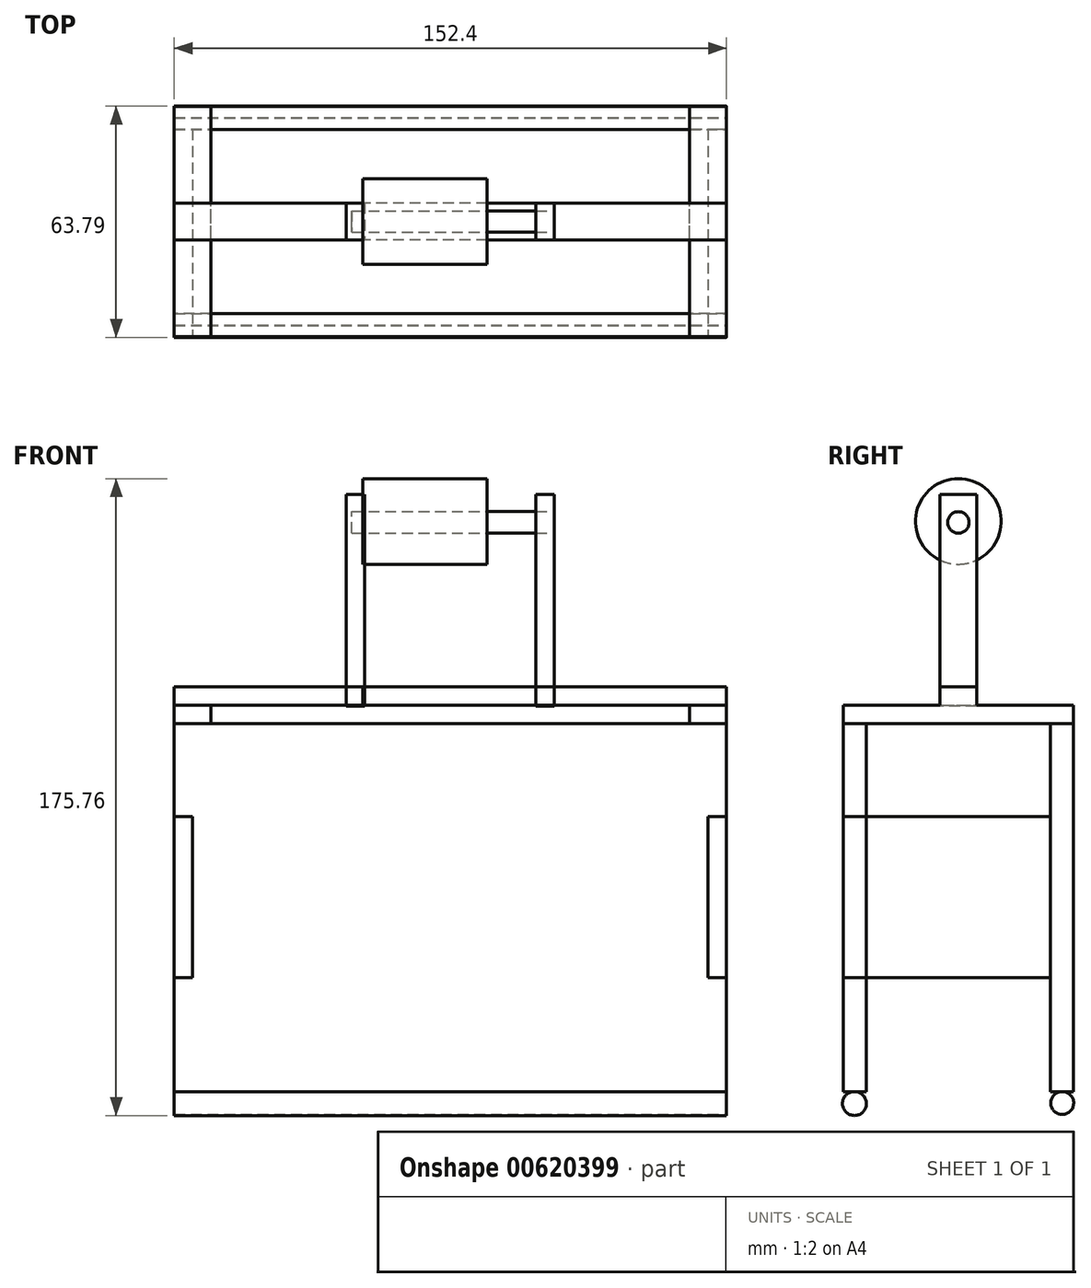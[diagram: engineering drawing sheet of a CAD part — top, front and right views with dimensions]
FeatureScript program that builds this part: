
annotation { "Feature Type Name" : "Feature", "Feature Type Description" : "" }
export const myFeature = defineFeature(function(context is Context, id is Id, definition is map)
    precondition{}
    {
        {
            var Q0;
            Q0=qCreatedBy(makeId("Front.planeOp"),FACE);
            var sketch = newSketch(context, id + "F0", { "sketchPlane" : qUnion([Q0])});
            skLineSegment(sketch, "E0.bottom", {"start": v(-52.07, 51.1) * mm, "end": v(100.33, 51.1) * mm});
            skLineSegment(sketch, "E0.top", {"start": v(-52.07, -50.5) * mm, "end": v(100.33, -50.5) * mm});
            skLineSegment(sketch, "E0.left", {"start": v(-52.07, 51.1) * mm, "end": v(-52.07, -50.5) * mm});
            skLineSegment(sketch, "E0.right", {"start": v(100.33, 51.1) * mm, "end": v(100.33, -50.5) * mm});
            skSolve(sketch);
        }
        {
            var Q0;
            Q0=makeQuery(id+"F0.imprint","IMPRINT",FACE,{"disambiguationData":[TD([[makeQuery(id+"F0.imprint","IMPRINT",EDGE,{"derivedFrom":sQuery(id+"F0.wireOp",EDGE,"E0.bottom")}),-1.0]])]});
            extrude(context, id + "F1", {"entities" : qUnion([Q0]), "depth" : 6.35 * mm, "offsetDistance" : 25.4 * mm});
        }
        {
            var Q0;
            Q0=qCreatedBy(makeId("Right.planeOp"),FACE);
            var sketch = newSketch(context, id + "F2", { "sketchPlane" : qUnion([Q0])});
            skLineSegment(sketch, "E1", {"start": v(-57.15, 0) * mm, "end": v(-57.15, 51.1) * mm});
            skLineSegment(sketch, "E2", {"start": v(-57.15, 51.1) * mm, "end": v(-63.5, 51.1) * mm});
            skLineSegment(sketch, "E3", {"start": v(-63.5, 51.1) * mm, "end": v(-63.5, -50.5) * mm});
            skLineSegment(sketch, "E4", {"start": v(-63.5, -50.5) * mm, "end": v(-57.15, -50.5) * mm});
            skLineSegment(sketch, "E5", {"start": v(-57.15, -50.5) * mm, "end": v(-57.15, 0) * mm});
            skLineSegment(sketch, "E6", {"start": v(-57.15, 51.1) * mm, "end": v(0, 51.1) * mm});
            skSolve(sketch);
        }
        {
            var Q0;
            Q0 = qSketchRegion(id + "F2", true);
            extrude(context, id + "F3", {"entities" : qUnion([Q0]), "depth" : 100.33 * mm, "offsetDistance" : 25.4 * mm});
        }
        {
            var Q0;
            Q0=makeQuery(id+"F3.opExtrude","CAP_FACE",FACE,{"disambiguationData":[OSD([sQuery(id+"F2.wireOp",EDGE,"E1"),sQuery(id+"F2.wireOp",EDGE,"E2"),sQuery(id+"F2.wireOp",EDGE,"E3"),sQuery(id+"F2.wireOp",EDGE,"E4"),sQuery(id+"F2.wireOp",EDGE,"E5")])],"isStart":true});
            extrude(context, id + "F4", {"entities" : qUnion([Q0]), "operationType" : NewBodyOperationType.ADD, "depth" : 52.07 * mm, "offsetDistance" : 25.4 * mm});
        }
        {
            var Q0;
            {var subQ0=sQuery(id+"F2.wireOp",EDGE,"E3");Q0=makeQuery(id+"F4.boolean.opBoolean","MERGE",FACE,{"derivedFrom":[makeQuery(id+"F3.opExtrude","SWEPT_FACE",FACE,{"disambiguationData":[OSD([subQ0])]}),makeQuery(id+"F4.opExtrude","SWEPT_FACE",FACE,{"disambiguationData":[OSD([subQ0])]})]});}
            var sketch = newSketch(context, id + "F5", { "sketchPlane" : qUnion([Q0])});
            skLineSegment(sketch, "E7", {"start": v(-52.07, 25.4) * mm, "end": v(-47, 25.4) * mm});
            skLineSegment(sketch, "E8", {"start": v(-47, 25.4) * mm, "end": v(-47, -19.05) * mm});
            skLineSegment(sketch, "E9", {"start": v(-47, -19.05) * mm, "end": v(-52.07, -19.05) * mm});
            skLineSegment(sketch, "E10", {"start": v(100.33, 25.4) * mm, "end": v(95.25, 25.4) * mm});
            skLineSegment(sketch, "E11", {"start": v(95.25, 25.4) * mm, "end": v(95.25, -19.05) * mm});
            skLineSegment(sketch, "E12", {"start": v(95.25, -19.05) * mm, "end": v(100.33, -19.05) * mm});
            skSolve(sketch);
        }
        {
            var Q0;
            {var subQ0=sQuery(id+"F5.wireOp",EDGE,"E7");Q0=makeQuery(id+"F5.imprint","IMPRINT",FACE,{"disambiguationData":[TD([[makeQuery(id+"F5.imprint","IMPRINT",EDGE,{"derivedFrom":subQ0}),-1.0]])]});}
            var Q1;
            {var subQ0=sQuery(id+"F5.wireOp",EDGE,"E10");Q1=makeQuery(id+"F5.imprint","IMPRINT",FACE,{"disambiguationData":[TD([[makeQuery(id+"F5.imprint","IMPRINT",EDGE,{"derivedFrom":subQ0}),1.0]])]});}
            extrude(context, id + "F6", {"entities" : qUnion([Q0, Q1]), "oppositeDirection" : true, "depth" : 57.15 * mm, "offsetDistance" : 25.4 * mm});
        }
        {
            var Q0;
            Q0=qCreatedBy(makeId("Front.planeOp"),FACE);
            var sketch = newSketch(context, id + "F7", { "sketchPlane" : qUnion([Q0])});
            skLineSegment(sketch, "E13.0", {"start": v(100.33, 51.1) * mm, "end": v(-52.07, 51.1) * mm});
            skLineSegment(sketch, "E14", {"start": v(-52.07, 51.1) * mm, "end": v(-52.07, 56.18) * mm});
            skLineSegment(sketch, "E15", {"start": v(-52.07, 56.18) * mm, "end": v(-41.91, 56.18) * mm});
            skLineSegment(sketch, "E16", {"start": v(-41.91, 56.18) * mm, "end": v(-41.91, 51.1) * mm});
            skLineSegment(sketch, "E17", {"start": v(100.33, 51.1) * mm, "end": v(100.33, 56.18) * mm});
            skLineSegment(sketch, "E18", {"start": v(100.33, 56.18) * mm, "end": v(90.17, 56.18) * mm});
            skLineSegment(sketch, "E19", {"start": v(90.17, 56.18) * mm, "end": v(90.17, 51.1) * mm});
            skSolve(sketch);
        }
        {
            var Q0;
            Q0 = qSketchRegion(id + "F7", true);
            extrude(context, id + "F8", {"entities" : qUnion([Q0]), "depth" : 63.5 * mm, "offsetDistance" : 25.4 * mm});
        }
        {
            var Q0;
            Q0=qCreatedBy(makeId("Right.planeOp"),FACE);
            var sketch = newSketch(context, id + "F9", { "sketchPlane" : qUnion([Q0])});
            skLineSegment(sketch, "E20.0", {"start": v(-63.5, 56.18) * mm, "end": v(0, 56.18) * mm});
            skLineSegment(sketch, "E21", {"start": v(-36.83, 56.18) * mm, "end": v(-36.83, 61.26) * mm});
            skLineSegment(sketch, "E22", {"start": v(-36.83, 61.26) * mm, "end": v(-26.67, 61.26) * mm});
            skLineSegment(sketch, "E23", {"start": v(-26.67, 61.26) * mm, "end": v(-26.67, 56.18) * mm});
            skSolve(sketch);
        }
        {
            var Q0;
            {var subQ0=sQuery(id+"F9.wireOp",EDGE,"E21");Q0=makeQuery(id+"F9.imprint","IMPRINT",FACE,{"disambiguationData":[TD([[makeQuery(id+"F9.imprint","IMPRINT",EDGE,{"derivedFrom":subQ0}),-1.0]])]});}
            extrude(context, id + "F10", {"entities" : qUnion([Q0]), "operationType" : NewBodyOperationType.ADD, "depth" : 100.33 * mm, "offsetDistance" : 25.4 * mm});
        }
        {
            var Q0;
            Q0=makeQuery(id+"F10.opExtrude","CAP_FACE",FACE,{"disambiguationData":[OSD([sQuery(id+"F9.wireOp",EDGE,"E20.0"),sQuery(id+"F9.wireOp",EDGE,"E21"),sQuery(id+"F9.wireOp",EDGE,"E22"),sQuery(id+"F9.wireOp",EDGE,"E23")])],"isStart":true});
            extrude(context, id + "F11", {"entities" : qUnion([Q0]), "depth" : 52.07 * mm, "offsetDistance" : 25.4 * mm});
        }
        {
            var Q0;
            Q0=qCreatedBy(makeId("Top.planeOp"),FACE);
            var sketch = newSketch(context, id + "F12", { "sketchPlane" : qUnion([Q0])});
            skLineSegment(sketch, "E24", {"start": v(47.75, -36.83) * mm, "end": v(47.75, -26.67) * mm});
            skLineSegment(sketch, "E25", {"start": v(47.75, -26.67) * mm, "end": v(52.83, -26.67) * mm});
            skLineSegment(sketch, "E26", {"start": v(52.83, -26.67) * mm, "end": v(52.83, -36.83) * mm});
            skLineSegment(sketch, "E27", {"start": v(52.83, -36.83) * mm, "end": v(47.75, -36.83) * mm});
            skLineSegment(sketch, "E28.bottom", {"start": v(-4.57, -26.67) * mm, "end": v(0.5, -26.67) * mm});
            skLineSegment(sketch, "E28.top", {"start": v(-4.57, -36.83) * mm, "end": v(0.5, -36.83) * mm});
            skLineSegment(sketch, "E28.left", {"start": v(-4.57, -26.67) * mm, "end": v(-4.57, -36.83) * mm});
            skLineSegment(sketch, "E28.right", {"start": v(0.5, -26.67) * mm, "end": v(0.5, -36.83) * mm});
            skSolve(sketch);
        }
        {
            var Q0;
            Q0=makeQuery(id+"F12.imprint","IMPRINT",FACE,{"disambiguationData":[TD([[makeQuery(id+"F12.imprint","IMPRINT",EDGE,{"derivedFrom":sQuery(id+"F12.wireOp",EDGE,"E28.bottom")}),-1.0]])]});
            var Q1;
            Q1=makeQuery(id+"F12.imprint","IMPRINT",FACE,{"disambiguationData":[TD([[makeQuery(id+"F12.imprint","IMPRINT",EDGE,{"derivedFrom":sQuery(id+"F12.wireOp",EDGE,"E24")}),-1.0]])]});
            extrude(context, id + "F13", {"entities" : qUnion([Q0, Q1]), "depth" : 114.3 * mm, "offsetDistance" : 25.4 * mm});
        }
        {
            var Q0;
            Q0=makeQuery(id+"F13.opExtrude","CAP_FACE",FACE,{"disambiguationData":[OSD([sQuery(id+"F12.wireOp",EDGE,"E28.bottom"),sQuery(id+"F12.wireOp",EDGE,"E28.top"),sQuery(id+"F12.wireOp",EDGE,"E28.left"),sQuery(id+"F12.wireOp",EDGE,"E28.right")])],"isStart":true});
            extrude(context, id + "F14", {"entities" : qUnion([Q0]), "operationType" : NewBodyOperationType.REMOVE, "oppositeDirection" : true, "depth" : 55.88 * mm, "offsetDistance" : 25.4 * mm});
        }
        {
            var Q0;
            Q0=makeQuery(id+"F13.opExtrude","CAP_FACE",FACE,{"disambiguationData":[OSD([sQuery(id+"F12.wireOp",EDGE,"E24"),sQuery(id+"F12.wireOp",EDGE,"E25"),sQuery(id+"F12.wireOp",EDGE,"E26"),sQuery(id+"F12.wireOp",EDGE,"E27")])],"isStart":true});
            extrude(context, id + "F15", {"entities" : qUnion([Q0]), "operationType" : NewBodyOperationType.REMOVE, "oppositeDirection" : true, "depth" : 55.88 * mm, "offsetDistance" : 25.4 * mm});
        }
        {
            var Q0;
            Q0=makeQuery(id+"F13.opExtrude","SWEPT_FACE",FACE,{"disambiguationData":[OSD([sQuery(id+"F12.wireOp",EDGE,"E26")])]});
            var sketch = newSketch(context, id + "F16", { "sketchPlane" : qUnion([Q0])});
            skCircle(sketch, "E29", {"center": v(-31.75, 106.58) * mm, "radius": 2.96 * mm});
            skCircle(sketch, "E30", {"center": v(-31.75, 106.58) * mm, "radius": 12.48 * mm});
            skSolve(sketch);
        }
        {
            var Q0;
            Q0=makeQuery(id+"F16.imprint","IMPRINT",FACE,{"disambiguationData":[TD([[makeQuery(id+"F16.imprint","IMPRINT",EDGE,{"derivedFrom":sQuery(id+"F16.wireOp",EDGE,"E29")}),1.0]])]});
            extrude(context, id + "F17", {"entities" : qUnion([Q0]), "oppositeDirection" : true, "depth" : 55.88 * mm, "offsetDistance" : 25.4 * mm});
        }
        {
            var Q0;
            Q0=qCreatedBy(makeId("Right.planeOp"),FACE);
            var sketch = newSketch(context, id + "F18", { "sketchPlane" : qUnion([Q0])});
            skCircle(sketch, "E31", {"center": v(-31.75, 106.85) * mm, "radius": 11.8 * mm});
            skLineSegment(sketch, "E32.0", {"start": v(-26.67, 114.3) * mm, "end": v(-26.67, 55.88) * mm});
            skSolve(sketch);
        }
        {
            var Q0;
            Q0=makeQuery(id+"F18.imprint","IMPRINT",FACE,{"disambiguationData":[TD([[makeQuery(id+"F18.imprint","IMPRINT",EDGE,{"derivedFrom":sQuery(id+"F18.wireOp",EDGE,"E31")}),1.0]])]});
            extrude(context, id + "F19", {"entities" : qUnion([Q0]), "depth" : 34.3 * mm, "offsetDistance" : 25.4 * mm});
        }
        {
            var Q0;
            Q0=makeQuery(id+"F3.opExtrude","CAP_FACE",FACE,{"disambiguationData":[OSD([sQuery(id+"F2.wireOp",EDGE,"E1"),sQuery(id+"F2.wireOp",EDGE,"E2"),sQuery(id+"F2.wireOp",EDGE,"E3"),sQuery(id+"F2.wireOp",EDGE,"E4"),sQuery(id+"F2.wireOp",EDGE,"E5")])],"isStart":false});
            var sketch = newSketch(context, id + "F20", { "sketchPlane" : qUnion([Q0])});
            skCircle(sketch, "E33", {"center": v(-60.42, -53.8) * mm, "radius": 3.3 * mm});
            skSolve(sketch);
        }
        {
            var Q0;
            {var subQ0=sQuery(id+"F20.wireOp",EDGE,"E33");var subQ1=makeQuery(id+"F3.opExtrude","CAP_EDGE",EDGE,{"disambiguationData":[OSD([sQuery(id+"F2.wireOp",EDGE,"E4")])],"isStart":false});var subQ2=makeQuery(id+"F20.imprint","INTERSECT",VERTEX,{"disambiguationData":[OD(0.0)],"derivedFrom":[subQ1,subQ0]});Q0=makeQuery(id+"F20.imprint","IMPRINT",FACE,{"disambiguationData":[TD([[makeQuery(id+"F20.imprint","IMPRINT",EDGE,{"disambiguationData":[TD([[subQ2,-1.0]])],"derivedFrom":subQ0}),1.0]])]});}
            var sketch = newSketch(context, id + "F21", { "sketchPlane" : qUnion([Q0])});
            skCircle(sketch, "E34", {"center": v(-3.1, -53.66) * mm, "radius": 3.16 * mm});
            skSolve(sketch);
        }
        {
            var Q0;
            Q0=makeQuery(id+"F21.imprint","IMPRINT",FACE,{"disambiguationData":[TD([[makeQuery(id+"F21.imprint","IMPRINT",EDGE,{"derivedFrom":sQuery(id+"F21.wireOp",EDGE,"E34")}),1.0]])]});
            extrude(context, id + "F22", {"entities" : qUnion([Q0]), "operationType" : NewBodyOperationType.ADD, "oppositeDirection" : true, "depth" : 152.4 * mm, "offsetDistance" : 25.4 * mm});
        }
        {
            var Q0;
            {var subQ0=sQuery(id+"F20.wireOp",EDGE,"E33");var subQ1=makeQuery(id+"F3.opExtrude","CAP_EDGE",EDGE,{"disambiguationData":[OSD([sQuery(id+"F2.wireOp",EDGE,"E4")])],"isStart":false});var subQ2=makeQuery(id+"F20.imprint","INTERSECT",VERTEX,{"disambiguationData":[OD(0.0)],"derivedFrom":[subQ1,subQ0]});Q0=makeQuery(id+"F20.imprint","IMPRINT",FACE,{"disambiguationData":[TD([[makeQuery(id+"F20.imprint","IMPRINT",EDGE,{"disambiguationData":[TD([[subQ2,-1.0]])],"derivedFrom":subQ0}),1.0]])]});}
            extrude(context, id + "F23", {"entities" : qUnion([Q0]), "operationType" : NewBodyOperationType.ADD, "oppositeDirection" : true, "depth" : 152.4 * mm, "offsetDistance" : 25.4 * mm});
        }
    });
